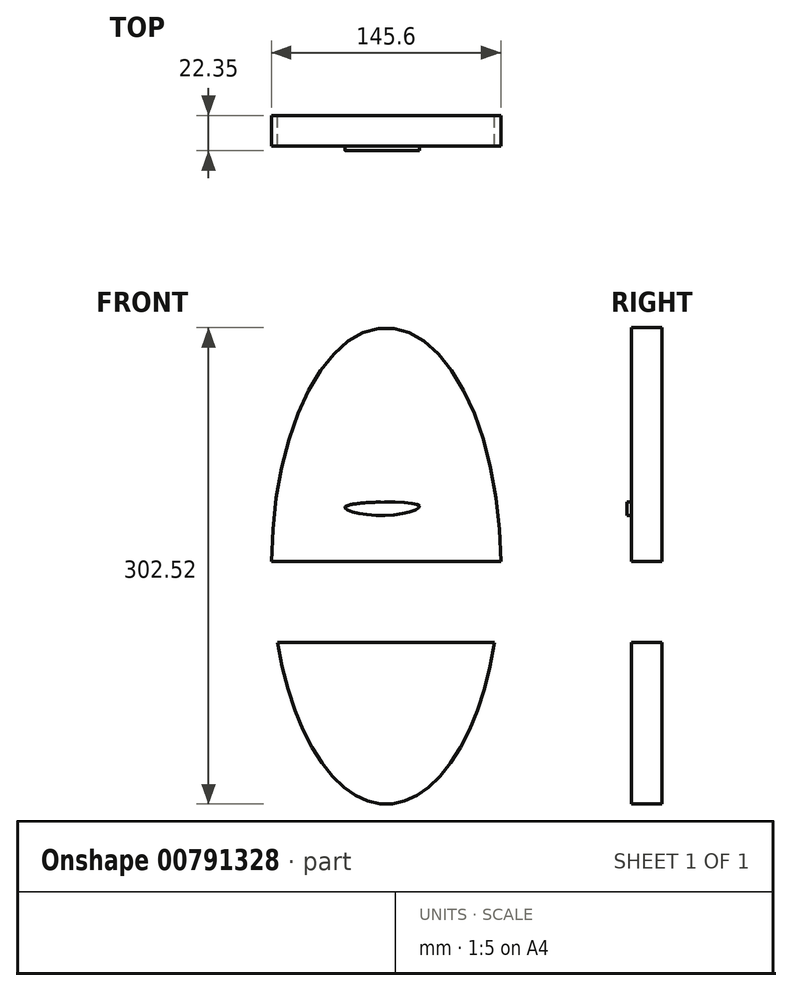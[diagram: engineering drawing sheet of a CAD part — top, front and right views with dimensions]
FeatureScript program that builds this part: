
annotation { "Feature Type Name" : "Feature", "Feature Type Description" : "" }
export const myFeature = defineFeature(function(context is Context, id is Id, definition is map)
    precondition{}
    {
        {
            var Q0;
            Q0=qCreatedBy(makeId("Front.planeOp"),FACE);
            var sketch = newSketch(context, id + "F0", { "sketchPlane" : qUnion([Q0])});
            skEllipse(sketch, "E0", {"center": v(0, -75.2) * mm, "majorRadius": 151.26 * mm, "minorRadius": 72.8 * mm, "majorAxis": v(0, 1)});
            skSolve(sketch);
        }
        {
            var Q0;
            Q0 = qSketchRegion(id + "F0", true);
            extrude(context, id + "F1", {"entities" : qUnion([Q0]), "depth" : 19.3 * mm, "offsetDistance" : 25.4 * mm});
        }
        {
            var Q0;
            Q0=qCreatedBy(makeId("Front.planeOp"),FACE);
            var sketch = newSketch(context, id + "F2", { "sketchPlane" : qUnion([Q0])});
            skLineSegment(sketch, "E1.bottom", {"start": v(-75.65, -72.39) * mm, "end": v(74.54, -72.39) * mm});
            skLineSegment(sketch, "E1.top", {"start": v(-75.65, -123.8) * mm, "end": v(74.54, -123.8) * mm});
            skLineSegment(sketch, "E1.left", {"start": v(-75.65, -72.39) * mm, "end": v(-75.65, -123.8) * mm});
            skLineSegment(sketch, "E1.right", {"start": v(74.54, -72.39) * mm, "end": v(74.54, -123.8) * mm});
            skSolve(sketch);
        }
        {
            var Q0;
            Q0=makeQuery(id+"F2.imprint","IMPRINT",FACE,{"disambiguationData":[TD([[makeQuery(id+"F2.imprint","IMPRINT",EDGE,{"derivedFrom":sQuery(id+"F2.wireOp",EDGE,"E1.bottom")}),-1.0]])]});
            extrude(context, id + "F3", {"entities" : qUnion([Q0]), "operationType" : NewBodyOperationType.REMOVE, "depth" : 22.6 * mm, "offsetDistance" : 25.4 * mm});
        }
        {
            var Q0;
            {var subQ0=sQuery(id+"F0.wireOp",EDGE,"E0");Q0=makeQuery(id+"F3.boolean.opBoolean","SPLIT",FACE,{"disambiguationData":[TD([makeQuery(id+"F3.opExtrude","SWEPT_FACE",FACE,{"disambiguationData":[OSD([sQuery(id+"F2.wireOp",EDGE,"E1.bottom")])]})])],"derivedFrom":makeQuery(id+"F1.opExtrude","CAP_FACE",FACE,{"disambiguationData":[OSD([subQ0])],"isStart":false})});}
            var sketch = newSketch(context, id + "F4", { "sketchPlane" : qUnion([Q0])});
            skFitSpline(sketch, "E2", {"points": [v(-25.67, -37.42) * mm, v(0, -43.18) * mm, v(20.61, -36.59) * mm, v(-25.67, -37.42) * mm]});
            skSolve(sketch);
        }
        {
            var Q0;
            Q0 = qSketchRegion(id + "F4", true);
            extrude(context, id + "F5", {"entities" : qUnion([Q0]), "operationType" : NewBodyOperationType.ADD, "depth" : 3.05 * mm, "offsetDistance" : 25.4 * mm});
        }
    });
